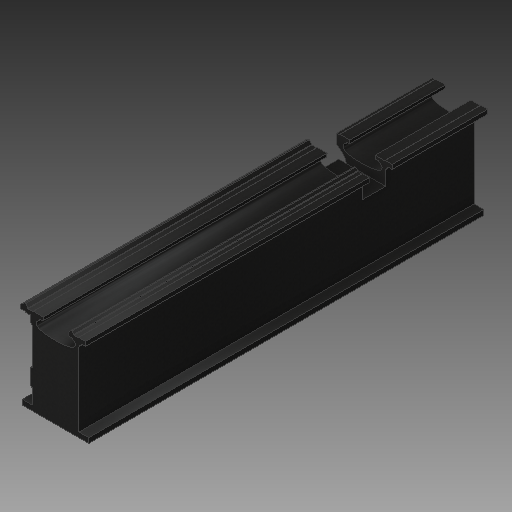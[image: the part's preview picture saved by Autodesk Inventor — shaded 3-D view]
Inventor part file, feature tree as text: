
AUTODESK INVENTOR PART (.ipt)
format: ipt  version: 2018 (Build 220112000, 112)  size: 437,248 bytes
history: native  units: in
note: dims shown in document units (in); Inventor stores cm internally (conversion verified against a paired STEP export)
features: extrude x11, sketch x11, reference x6, plane x3, chamfer x1
ambient origin geometry x8: Origin, YZ Plane, XZ Plane, XY Plane, X Axis, Y Axis, Z Axis, Center Point
bodies: Solid1 (feature_tree)
feature tree (32):
  extrude  "Extrusion1"  TaperAngle=150.0deg  [1 undecoded]
  chamfer  "Chamfer1"  Distance=0.9921in
  plane  "Work Plane3"
  extrude  "Extrusion2"  Depth=0.7874in
  extrude  "Extrusion3"  Depth=0.7874in
  extrude  "Extrusion4"  Depth=0.7874in
  extrude  "Extrusion5"  TaperAngle=120.0deg  [1 undecoded]
  extrude  "Extrusion6"  Depth=0.1575in
  extrude  "Extrusion7"  Depth=0.7874in
  extrude  "Extrusion8"  Depth=0.7874in
  plane  "Work Plane4"
  plane  "Work Plane5"
  extrude  "Extrusion9"  Depth=0.7874in
  extrude  "Extrusion10"  Depth=0.7874in
  extrude  "Extrusion11"  Depth=0.7874in
  sketch  "Sketch1"  dims[d0=0.4331in d1=150.0deg]
  sketch  "Sketch2"  dims[d2=0.3937in]
  sketch  "Sketch3"  dims[d3=0.4606in]
  sketch  "Sketch4"  dims[d4=0.4961in]
  sketch  "Sketch5"  dims[d5=0.962in]
  sketch  "Sketch6"  dims[d6=0.1496in]
  sketch  "Sketch8"  dims[d7=0.4016in]
  sketch  "Sketch9"  dims[d8=0.962in]
  sketch  "Sketch10"  dims[d9=0.126in]
  sketch  "Sketch11"  dims[d10=0.6339in]
  sketch  "Sketch12"  dims[d11=0.0787in d12=0.9921in d13=0.6181in d14=0.5787in d15=0.315in d16=120.0deg d17=0.1575in d18=2.4409in d19=8.0315in d22=3.6299in d24=0.5in d25=1.4252in d26=180.0deg d27=0.0787in d28=0.748in d29=0.0787in d30=0.5197in d31=0.962in d32=0.1811in d33=0.6299in d34=0.962in d35=0.5512in d36=0.5512in d37=90.0deg d38=0.1181in d39=60.0deg d40=0.685in d41=0.8858in d43=5.2953in d44=90.0deg d46=2.185in d47=90.0deg d50=90.0deg d51=1.378in d52=180.0deg d53=0.7087in d54=90.0deg d55=1.378in d57=0.7087in d59=180.0deg d60=0.315in d61=120.0deg d62=2.4409in d63=55.9055in d64=0.0in d65=0.1575in d66=0.0787in d67=45.0deg d68=40.1575in d69=3.2283in d70=3.4528in d71=55.9055in d72=0.0in d73=55.9055in d74=0.0in d75=55.9055in d76=0.0in d77=3.3465in d78=1.2205in d79=1.7323in d80=55.9055in d81=0.0in d82=1.0236in d83=0.0in d84=0.315in d85=0.315in d86=0.7283in d87=0.5512in d88=0.5118in d89=0.3937in d90=0.0in d91=0.315in d92=0.315in d93=6.7717in d94=0.8858in d95=0.5512in d96=0.7874in d97=0.0in d98=0.2756in d99=0.3937in d100=0.0in d101=5.5118in d102=1.9685in d103=0.2756in d104=1.5748in d105=0.0787in d106=0.0in d107=0.7874in d108=0.0in]
  reference  "Reference1"
  reference  "Reference2"
  reference  "Reference3"
  reference  "Reference4"
  reference  "Reference5"
  reference  "Reference6"
note: 2 required parameter values undecoded (feature->parameter linkage not recoverable at this tier; creation-order binding heuristic only, values carry confidence <= 0.55)
